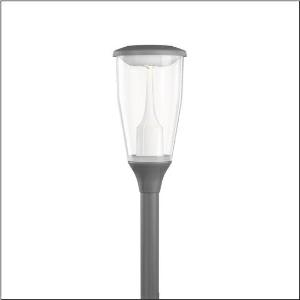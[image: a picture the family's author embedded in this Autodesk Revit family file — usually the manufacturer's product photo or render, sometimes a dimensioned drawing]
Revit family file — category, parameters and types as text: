
# Revit family: dl_11_iq___st1_2a_5xa5575ef14h000022_0b87
name_source: partatom
category: Lighting Fixtures
units: mm (PartAtom-declared; Revit-internal decimal feet)

## family parameters
Cut with Voids When Loaded = No
Host = Face
Light Source = No
Part Type = Normal
Room Calculation Point = No
Round Connector Dimension = Use Diameter
Shared = No

## types (1)
- --- (1 x LED, 1560 lm, 10.5 W, 3000K)
    Apparent Load = 11 VA
    CIE Flux Codes = 24 63 94 96 100
    Color Rendering = 70
    Color Temperature = 3000K
    Default Elevation = 1800 mm
    Description = DL 11 iQ, mast luminaire, Module 540 iQ-SR, primary light control with 3 zone facetted reflector, of plastic, silver coated, highly specular, structured, primary optical cover: cover, of PMMA, transparent, light distribution: ST1.2a, light emission: direct distribution, primary light characteristic: asymmetric, installation type: post-top, LED, High Power LED, rated luminous flux: 1.560lm, luminous efficacy: 149lm/W, light colour: 730, colour temperature: 3000K, control gear: iQ Street-Remote, control: Street-Remote, Auto-Match, Temp-Guard, Lumen-Switch, Night-Set, Smart-Wire, Light-Fading, Desk-Remote (wireless, voltage-free reading and setting of iQ features in the workshop via application-optimized NFC function/RFID function), optimised constant luminous flux control (CLO 2.0), mains connection: 220..240V, AC, 50/60Hz, connection cable pre-assembled, cable length: 5,5m, start of lifetime: 11W, end of service life: 11W, reduction: 5W, luminaire housing, upper part, of diecast aluminium, coated, SITECO metallic grey (DB 702S), spigot size: 76mm (post-top), mounting height: 3..5m, post-top mast mounting element, of diecast aluminium, coated, SITECO metallic grey (DB 702S), Module 540 iQ-SR, traffic white (RAL 9016), equipment: standard, protection rating (complete): IP66, insulation class (complete): insulation class II (safety insulation), certification: CE, ENEC, ENEC+, VDE, impact resistance: IK07, packaging unit: 1 piece

Light Distribution: ST1.2a
    Height = 665 mm
    Lamp = 1 x LED
    Lamp Light Flux = 1560 lm
    Lamp Power = 10.5 W
    Lamp count = 1
    Length = 334 mm
    Luminous efficacy = 149 lm/W
    Manufacturer = Siteco
    ModVariant = No
    Model = 5XA5575EF14H000022
    Mounting Place = Pole
    Mounting Type = Pole top
    Number of Poles = 1
    OnlyDefault = Yes
    Power Factor = 1
    Product Name = DL 11 iQ | ST1.2a
    Product group = mast luminaire | pylon top
    ProductGroupID = 6100
    Protection Class = Protection class II
    Protection Degree = IP 66
    RLX_Detail_Level = 1
    RLX_Emergency_Light_Flux = 0 lm
    RLX_Emergency_Type = 0
    RLX_Emergency_Type_DB = No
    RlxData = <blob elided: 153157 chars, md5=8e17a598>
    Socket = socket
    Standby Power = 0 W
    System Light Flux = 1560 lm
    System Power = 11 W
    Type Comments = factory setting: luminous flux: 100 % | dim-lin: 254 | 419 mA
    Type Image = l_1258354.jpg
    URL = http://relux.com
    VarID = @adj_100379
    Voltage = 0 V
    Weight = 0.00 kg
    Width = 0 mm  [stored 0 ft]

note: [stored X ft] marks values corroborated as IEEE doubles in the binary element streams (Revit-internal decimal feet)

## geometry (parser evidence)
native form markers: Blend x4, Sweep x9
no freeform markers — native parametric forms only
